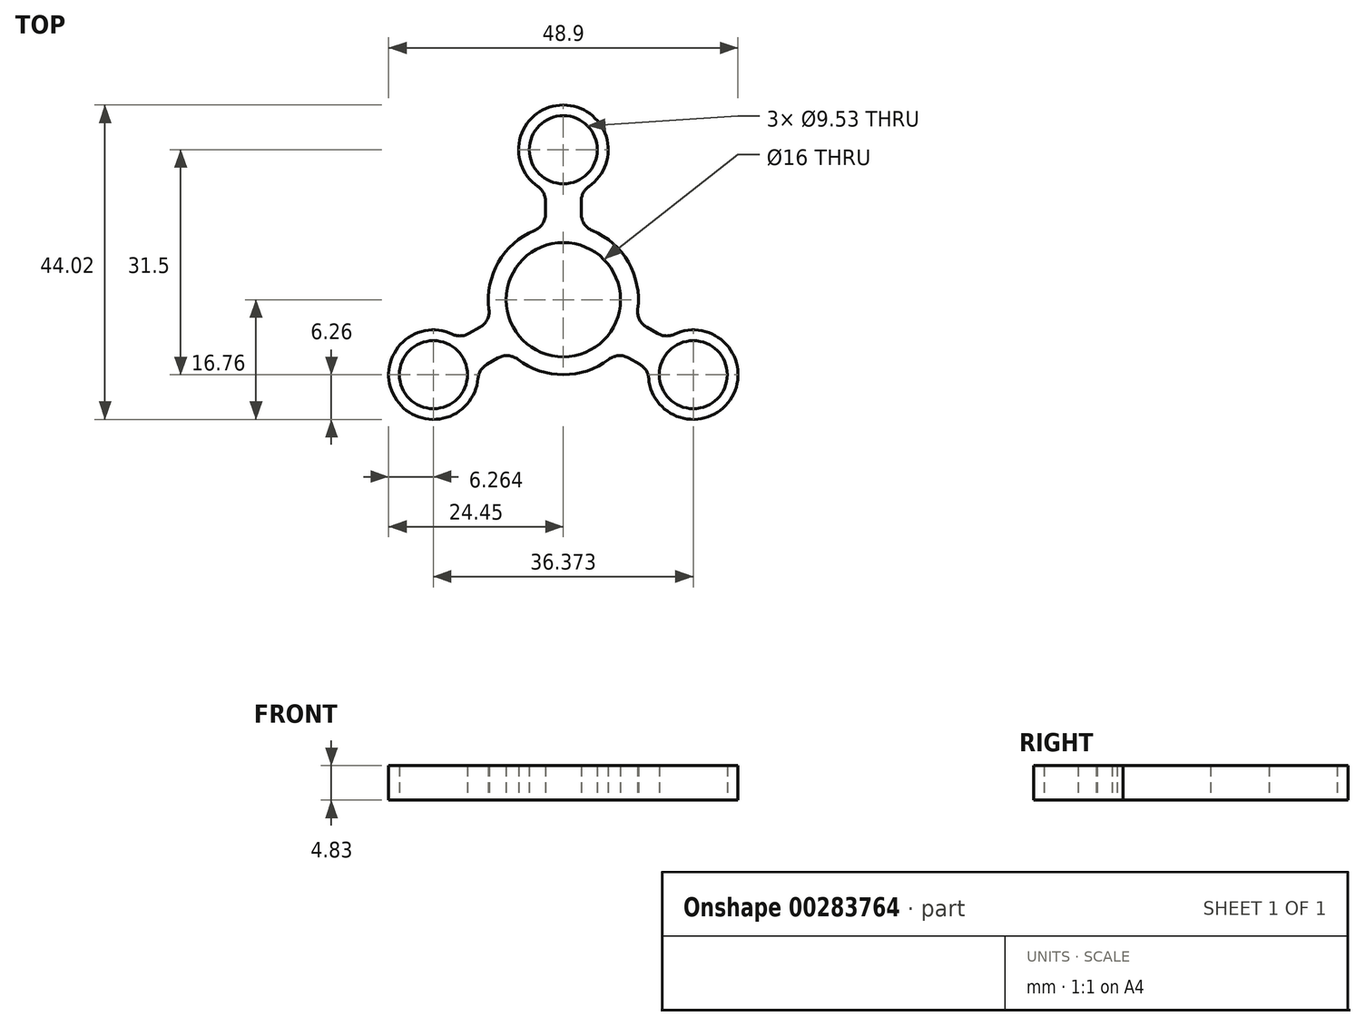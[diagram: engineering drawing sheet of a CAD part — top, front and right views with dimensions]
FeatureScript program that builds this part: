
annotation { "Feature Type Name" : "Feature", "Feature Type Description" : "" }
export const myFeature = defineFeature(function(context is Context, id is Id, definition is map)
    precondition{}
    {
        {
            var Q0;
            Q0=qCreatedBy(makeId("Top.planeOp"),FACE);
            var sketch = newSketch(context, id + "F0", { "sketchPlane" : qUnion([Q0])});
            skCircle(sketch, "E0", {"center": v(0, 0) * mm, "radius": 8 * mm});
            skPoint(sketch, "E1.middle", {"position": v(0, 10) * mm});
            skCircle(sketch, "E2", {"center": v(0, 21) * mm, "radius": 4.76 * mm});
            skArc(sketch, "E3.0", {"start": v(3.57, 15.86) * mm, "mid": v(0, 27.26) * mm, "end": v(-3.57, 15.86) * mm});
            skLineSegment(sketch, "E4.trimOffspring", {"start": v(-2.5, 13.8) * mm, "end": v(-2.5, 12) * mm});
            skLineSegment(sketch, "E5.trimOffspring", {"start": v(2.5, 13.8) * mm, "end": v(2.5, 12) * mm});
            skArc(sketch, "E6.0", {"start": v(-4.04, 9.7) * mm, "mid": v(-9.1, 5.25) * mm, "end": v(-10.41, -1.35) * mm});
            skPoint(sketch, "E7.visualSharp", {"position": v(-2.5, 15.26) * mm});
            skArc(sketch, "E7.filletArc", {"start": v(-2.5, 13.8) * mm, "mid": v(-2.78, 14.96) * mm, "end": v(-3.57, 15.86) * mm});
            skPoint(sketch, "E8.visualSharp", {"position": v(2.5, 15.26) * mm});
            skArc(sketch, "E8.filletArc", {"start": v(3.57, 15.86) * mm, "mid": v(2.78, 14.96) * mm, "end": v(2.5, 13.8) * mm});
            skPoint(sketch, "E9.visualSharp", {"position": v(-2.5, 10.2) * mm});
            skArc(sketch, "E9.filletArc", {"start": v(-4.04, 9.7) * mm, "mid": v(-2.92, 10.61) * mm, "end": v(-2.5, 12) * mm});
            skPoint(sketch, "E10.visualSharp", {"position": v(2.5, 10.2) * mm});
            skArc(sketch, "E10.filletArc", {"start": v(2.5, 12) * mm, "mid": v(2.92, 10.61) * mm, "end": v(4.04, 9.7) * mm});
            skArc(sketch, "E11.1.0", {"start": v(-15.52, -4.83) * mm, "mid": v(-23.61, -13.63) * mm, "end": v(-11.95, -11.02) * mm});
            skPoint(sketch, "E11.1.1", {"position": v(-8.66, -5) * mm});
            skPoint(sketch, "E11.1.2", {"position": v(-10.08, -2.93) * mm});
            skPoint(sketch, "E11.1.3", {"position": v(-7.58, -7.26) * mm});
            skCircle(sketch, "E11.1.4", {"center": v(-18.19, -10.5) * mm, "radius": 4.76 * mm});
            skPoint(sketch, "E11.1.5", {"position": v(-11.96, -9.8) * mm});
            skPoint(sketch, "E11.1.6", {"position": v(-14.46, -5.46) * mm});
            skArc(sketch, "E11.1.7", {"start": v(-10.7, -9.07) * mm, "mid": v(-11.57, -9.9) * mm, "end": v(-11.95, -11.02) * mm});
            skArc(sketch, "E11.1.8", {"start": v(-15.52, -4.83) * mm, "mid": v(-14.35, -5.07) * mm, "end": v(-13.2, -4.74) * mm});
            skArc(sketch, "E11.1.9", {"start": v(-6.37, -8.34) * mm, "mid": v(-7.73, -7.84) * mm, "end": v(-9.14, -8.17) * mm});
            skArc(sketch, "E11.1.10", {"start": v(-11.64, -3.83) * mm, "mid": v(-10.65, -2.78) * mm, "end": v(-10.41, -1.35) * mm});
            skLineSegment(sketch, "E11.1.11", {"start": v(-13.2, -4.74) * mm, "end": v(-11.64, -3.83) * mm});
            skLineSegment(sketch, "E11.1.12", {"start": v(-10.7, -9.07) * mm, "end": v(-9.14, -8.17) * mm});
            skArc(sketch, "E11.2.0", {"start": v(11.95, -11.02) * mm, "mid": v(23.61, -13.63) * mm, "end": v(15.52, -4.83) * mm});
            skPoint(sketch, "E11.2.1", {"position": v(8.66, -5) * mm});
            skPoint(sketch, "E11.2.2", {"position": v(7.58, -7.26) * mm});
            skPoint(sketch, "E11.2.3", {"position": v(10.08, -2.93) * mm});
            skCircle(sketch, "E11.2.4", {"center": v(18.19, -10.5) * mm, "radius": 4.76 * mm});
            skPoint(sketch, "E11.2.5", {"position": v(14.46, -5.46) * mm});
            skPoint(sketch, "E11.2.6", {"position": v(11.96, -9.8) * mm});
            skArc(sketch, "E11.2.7", {"start": v(13.2, -4.74) * mm, "mid": v(14.35, -5.07) * mm, "end": v(15.52, -4.83) * mm});
            skArc(sketch, "E11.2.8", {"start": v(11.95, -11.02) * mm, "mid": v(11.57, -9.9) * mm, "end": v(10.7, -9.07) * mm});
            skArc(sketch, "E11.2.9", {"start": v(10.41, -1.35) * mm, "mid": v(10.65, -2.78) * mm, "end": v(11.64, -3.83) * mm});
            skArc(sketch, "E11.2.10", {"start": v(9.14, -8.17) * mm, "mid": v(7.73, -7.84) * mm, "end": v(6.37, -8.34) * mm});
            skLineSegment(sketch, "E11.2.11", {"start": v(10.7, -9.07) * mm, "end": v(9.14, -8.17) * mm});
            skLineSegment(sketch, "E11.2.12", {"start": v(13.2, -4.74) * mm, "end": v(11.64, -3.83) * mm});
            skArc(sketch, "E12.trimOffspring", {"start": v(-6.37, -8.34) * mm, "mid": v(0, -10.5) * mm, "end": v(6.37, -8.34) * mm});
            skArc(sketch, "E13.trimOffspring", {"start": v(10.41, -1.35) * mm, "mid": v(9.1, 5.25) * mm, "end": v(4.04, 9.7) * mm});
            skSolve(sketch);
        }
        {
            var Q0;
            Q0=makeQuery(id+"F0.imprint","IMPRINT",FACE,{"disambiguationData":[TD([[makeQuery(id+"F0.imprint","IMPRINT",EDGE,{"derivedFrom":sQuery(id+"F0.wireOp",EDGE,"E0")}),-1.0]])]});
            extrude(context, id + "F1", {"entities" : qUnion([Q0]), "depth" : 4.83 * mm, "offsetDistance" : 25 * mm});
        }
    });
